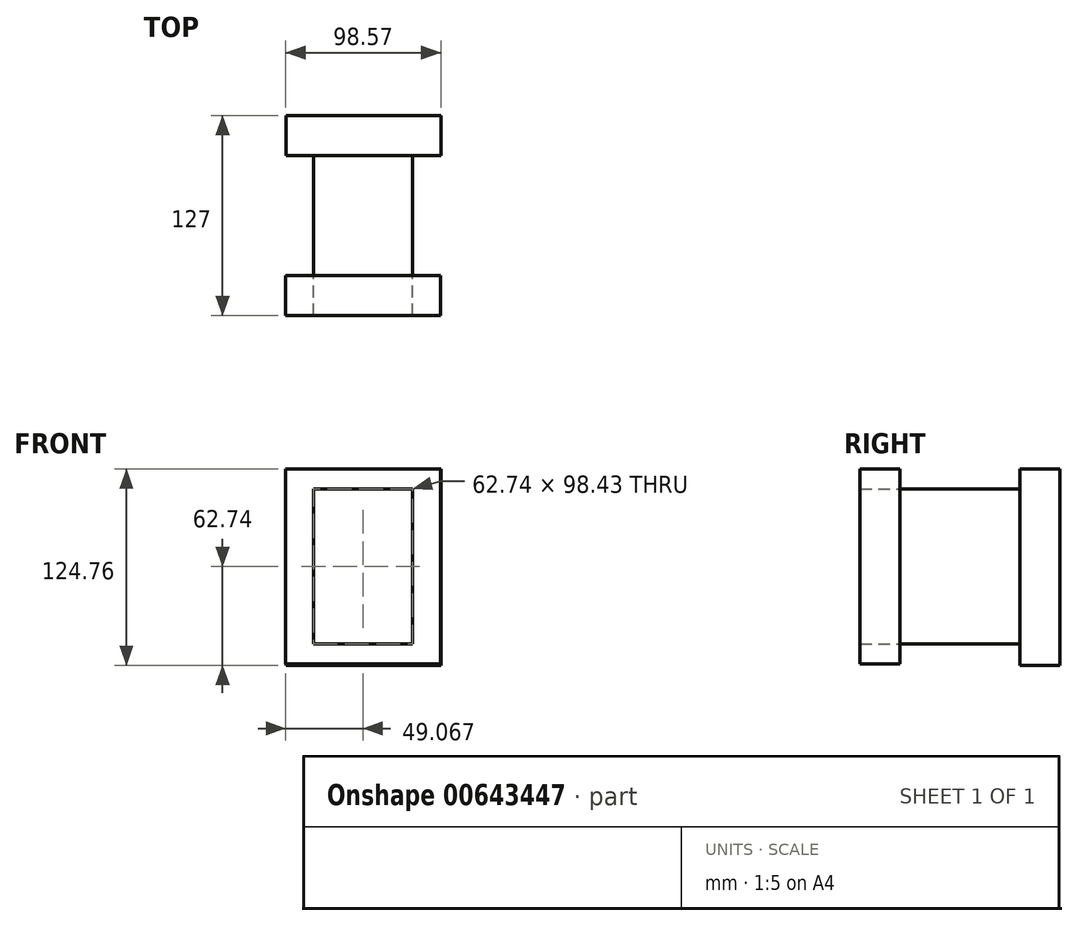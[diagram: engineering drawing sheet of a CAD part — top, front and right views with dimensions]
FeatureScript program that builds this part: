
annotation { "Feature Type Name" : "Feature", "Feature Type Description" : "" }
export const myFeature = defineFeature(function(context is Context, id is Id, definition is map)
    precondition{}
    {
        {
            var Q0;
            Q0=qCreatedBy(makeId("Front.planeOp"),FACE);
            var sketch = newSketch(context, id + "F0", { "sketchPlane" : qUnion([Q0])});
            skLineSegment(sketch, "E0.bottom", {"start": v(-64.9, 58.57) * mm, "end": v(33.53, 58.57) * mm});
            skLineSegment(sketch, "E0.top", {"start": v(-64.9, -66.05) * mm, "end": v(33.53, -66.05) * mm});
            skLineSegment(sketch, "E0.left", {"start": v(-64.9, 58.57) * mm, "end": v(-64.9, -66.05) * mm});
            skLineSegment(sketch, "E0.right", {"start": v(33.53, 58.57) * mm, "end": v(33.53, -66.05) * mm});
            skSolve(sketch);
        }
        {
            var Q0;
            Q0 = qSketchRegion(id + "F0", true);
            extrude(context, id + "F1", {"entities" : qUnion([Q0]), "depth" : 25.4 * mm, "offsetDistance" : 25.4 * mm});
        }
        {
            var Q0;
            Q0=qCreatedBy(makeId("Front.planeOp"),FACE);
            var sketch = newSketch(context, id + "F2", { "sketchPlane" : qUnion([Q0])});
            skLineSegment(sketch, "E1.bottom", {"start": v(-47.34, 45.9) * mm, "end": v(15.4, 45.9) * mm});
            skLineSegment(sketch, "E1.top", {"start": v(-47.34, -52.52) * mm, "end": v(15.4, -52.52) * mm});
            skLineSegment(sketch, "E1.left", {"start": v(-47.34, 45.9) * mm, "end": v(-47.34, -52.52) * mm});
            skLineSegment(sketch, "E1.right", {"start": v(15.4, 45.9) * mm, "end": v(15.4, -52.52) * mm});
            skSolve(sketch);
        }
        {
            var Q0;
            Q0 = qSketchRegion(id + "F2", true);
            extrude(context, id + "F3", {"entities" : qUnion([Q0]), "operationType" : NewBodyOperationType.ADD, "depth" : 101.6 * mm, "offsetDistance" : 25.4 * mm});
        }
        {
            var Q0;
            Q0=makeQuery(id+"F3.opExtrude","CAP_FACE",FACE,{"disambiguationData":[OSD([sQuery(id+"F2.wireOp",EDGE,"E1.bottom"),sQuery(id+"F2.wireOp",EDGE,"E1.top"),sQuery(id+"F2.wireOp",EDGE,"E1.left"),sQuery(id+"F2.wireOp",EDGE,"E1.right")])],"isStart":false});
            var sketch = newSketch(context, id + "F4", { "sketchPlane" : qUnion([Q0])});
            skLineSegment(sketch, "E2.bottom", {"start": v(-65.04, -65.04) * mm, "end": v(33.39, -65.04) * mm});
            skLineSegment(sketch, "E2.top", {"start": v(-65.04, 58.71) * mm, "end": v(33.39, 58.71) * mm});
            skLineSegment(sketch, "E2.left", {"start": v(-65.04, -65.04) * mm, "end": v(-65.04, 58.71) * mm});
            skLineSegment(sketch, "E2.right", {"start": v(33.39, -65.04) * mm, "end": v(33.39, 58.71) * mm});
            skLineSegment(sketch, "E3.bottom", {"start": v(-47.34, 45.9) * mm, "end": v(15.4, 45.9) * mm});
            skLineSegment(sketch, "E3.top", {"start": v(-47.34, -52.52) * mm, "end": v(15.4, -52.52) * mm});
            skLineSegment(sketch, "E3.left", {"start": v(-47.34, 45.9) * mm, "end": v(-47.34, -52.52) * mm});
            skLineSegment(sketch, "E3.right", {"start": v(15.4, 45.9) * mm, "end": v(15.4, -52.52) * mm});
            skSolve(sketch);
        }
        {
            var Q0;
            Q0 = qSketchRegion(id + "F4", true);
            extrude(context, id + "F5", {"entities" : qUnion([Q0]), "depth" : 25.4 * mm, "offsetDistance" : 25.4 * mm});
        }
    });
